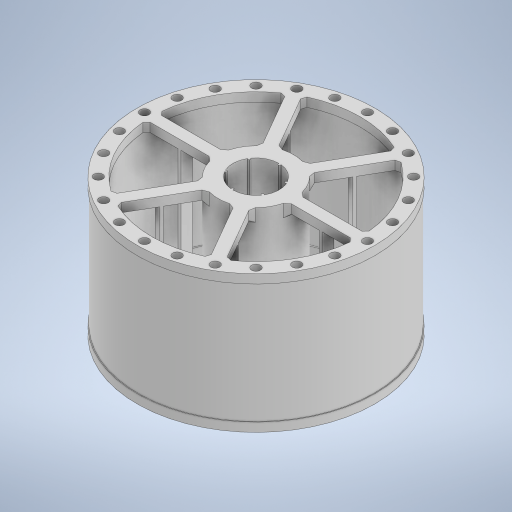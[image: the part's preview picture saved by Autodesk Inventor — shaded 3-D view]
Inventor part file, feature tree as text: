
AUTODESK INVENTOR PART (.ipt)
format: ipt  version: 2024 (Build 280153000, 153)  size: 596,480 bytes
history: native  units: mm
features: extrude x7, sketch x7, pattern_circular x4, chamfer x2, mirror x2, fillet x1
ambient origin geometry x8: Origin, YZ Plane, XZ Plane, XY Plane, X Axis, Y Axis, Z Axis, Center Point
bodies: Volumenkörper1 (feature_tree)
feature tree (23):
  extrude  "Extrusion1"  Depth=25.5mm
  extrude  "Extrusion2"  Depth=70.0mm
  extrude  "Extrusion4"  Depth=3.0mm TaperAngle=0.0deg
  chamfer  "Fasen1"  Distance=3.0mm
  mirror  "Spiegeln2"
  pattern_circular  "Runde Anordnung2"  Count=6 Angle=360.0deg
  chamfer  "Fasen2"  Distance=1.25mm Angle=45.0deg
  extrude  "Extrusion5"  Depth=40.2mm TaperAngle=0.0deg
  pattern_circular  "Runde Anordnung3"  Count=24 Angle=360.0deg
  mirror  "Spiegeln3"
  extrude  "Extrusion6"  Depth=40.2mm
  pattern_circular  "Runde Anordnung4"  [2 undecoded]
  fillet  "Rundung1"  Radius=46.2mm
  extrude  "Extrusion7"  Depth=40.2mm TaperAngle=360.0deg
  extrude  "Extrusion8"  Depth=40.2mm
  pattern_circular  "Runde Anordnung5"  [2 undecoded]
  sketch  "Skizze1"  dims[d2=15.5mm d3=25.5mm]
  sketch  "Skizze3"  dims[d4=46.2mm d5=0.0mm d6=70.0mm]
  sketch  "Skizze4"  dims[d7=80.0mm d8=3.0mm d9=0.0mm]
  sketch  "Skizze5"  dims[d13=0.3mm]
  sketch  "Skizze6"  dims[d21=2.0mm d22=3.0mm d23=0.0mm]
  sketch  "Skizze7"  dims[d24=1.25mm d25=2.0mm d26=45.0deg d27=60.0mm d28=360.0deg d30=1.25mm d31=2.0mm d32=45.0deg]
  sketch  "Skizze8"  dims[d33=3.0mm d34=3.0mm d35=0.0mm d36=240.0mm d37=360.0deg d39=0.63mm d40=0.75mm d41=46.2mm d42=0.0mm d43=60.0mm d44=360.0deg d46=0.35mm d47=79.5mm d48=78.5mm d49=40.2mm d50=0.0mm d51=70.8mm d52=71.8mm d53=0.5mm d54=1.0mm d55=40.2mm d56=0.0mm d57=60.0mm d58=360.0deg]
note: 4 required parameter values undecoded (feature->parameter linkage not recoverable at this tier; creation-order binding heuristic only, values carry confidence <= 0.55)
